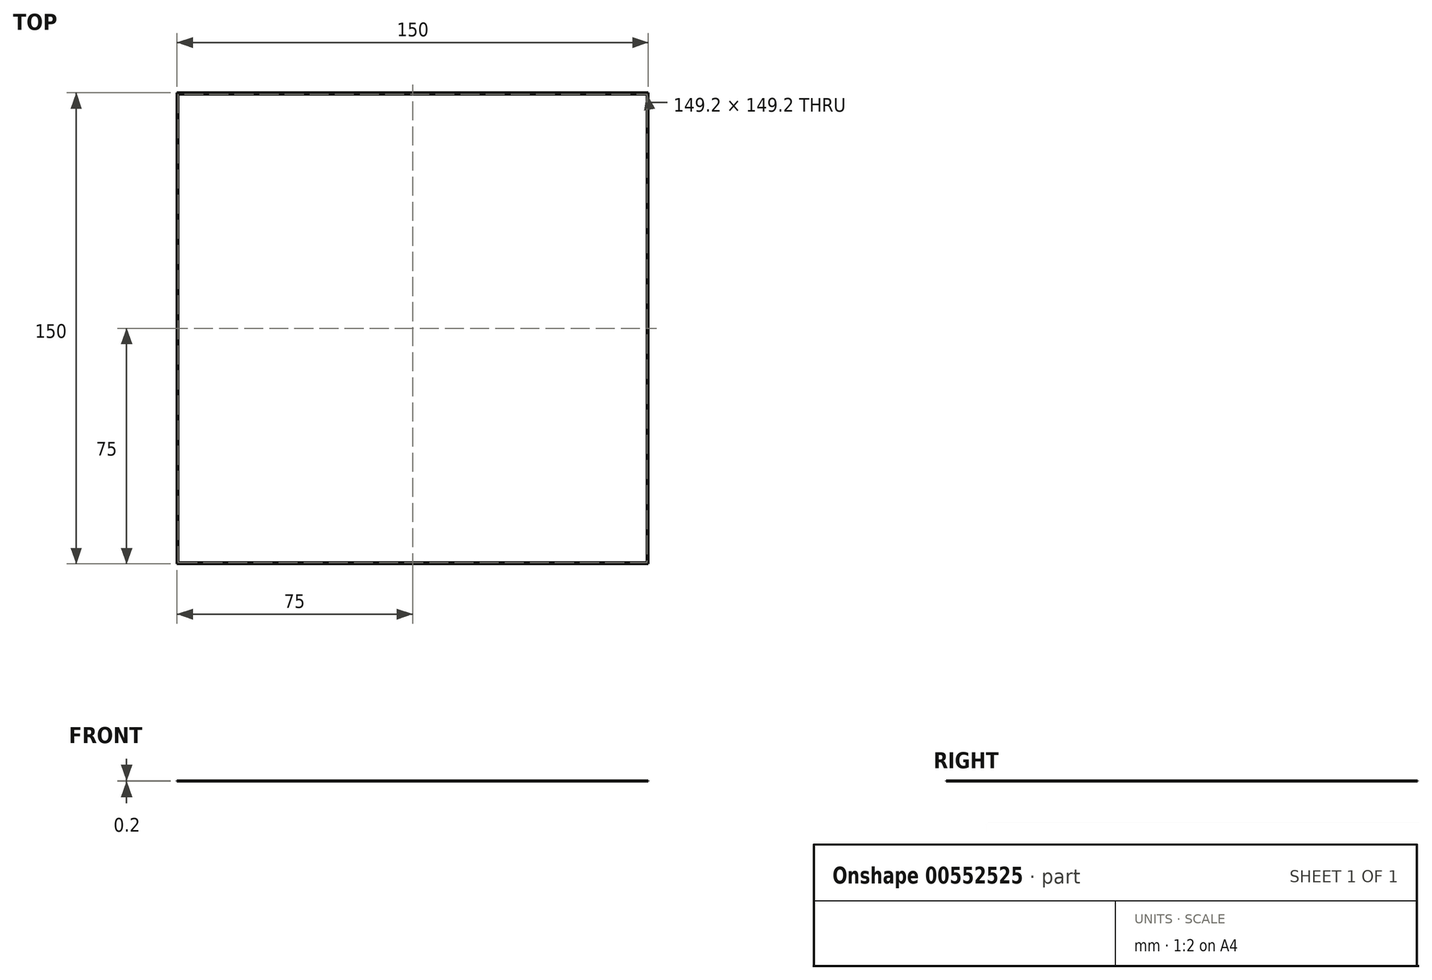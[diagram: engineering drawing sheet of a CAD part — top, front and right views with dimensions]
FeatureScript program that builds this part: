
annotation { "Feature Type Name" : "Feature", "Feature Type Description" : "" }
export const myFeature = defineFeature(function(context is Context, id is Id, definition is map)
    precondition{}
    {
        {
            var Q0;
            Q0=qCreatedBy(makeId("Top.planeOp"),FACE);
            var sketch = newSketch(context, id + "F0", { "sketchPlane" : qUnion([Q0])});
            skLineSegment(sketch, "E0.bottom", {"start": v(0, 0) * mm, "end": v(150, 0) * mm});
            skLineSegment(sketch, "E0.top", {"start": v(0, 150) * mm, "end": v(150, 150) * mm});
            skLineSegment(sketch, "E0.left", {"start": v(0, 0) * mm, "end": v(0, 150) * mm});
            skLineSegment(sketch, "E0.right", {"start": v(150, 0) * mm, "end": v(150, 150) * mm});
            skLineSegment(sketch, "E1.0", {"start": v(0.4, 0.4) * mm, "end": v(0.4, 149.6) * mm});
            skLineSegment(sketch, "E1.1", {"start": v(0.4, 0.4) * mm, "end": v(149.6, 0.4) * mm});
            skLineSegment(sketch, "E1.2", {"start": v(149.6, 0.4) * mm, "end": v(149.6, 149.6) * mm});
            skLineSegment(sketch, "E1.3", {"start": v(0.4, 149.6) * mm, "end": v(149.6, 149.6) * mm});
            skSolve(sketch);
        }
        {
            var Q0;
            Q0 = qSketchRegion(id + "F0", true);
            extrude(context, id + "F1", {"entities" : qUnion([Q0]), "depth" : .2 * mm, "offsetDistance" : 25.4 * mm});
        }
    });
